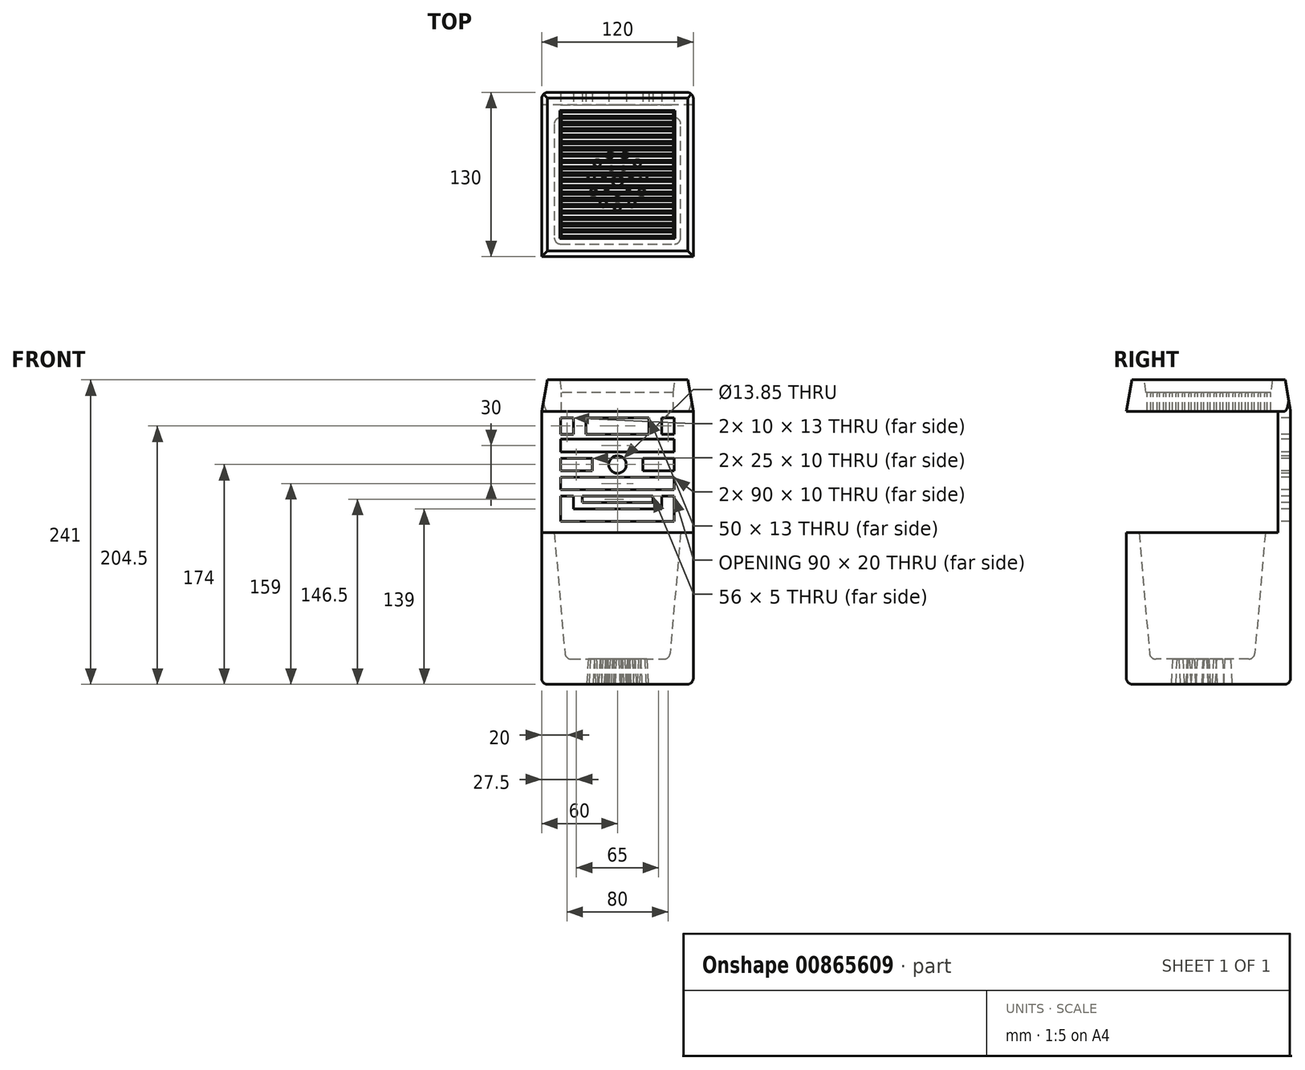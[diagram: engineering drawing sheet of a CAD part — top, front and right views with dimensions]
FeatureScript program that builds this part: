
annotation { "Feature Type Name" : "Feature", "Feature Type Description" : "" }
export const myFeature = defineFeature(function(context is Context, id is Id, definition is map)
    precondition{}
    {
        {
            assignVariable(context, id + "F0", {"name" : "length", "anyValue" : 120});
        }
        {
            var Q0;
            Q0=qCreatedBy(makeId("Top.planeOp"),FACE);
            var sketch = newSketch(context, id + "F1", { "sketchPlane" : qUnion([Q0])});
            skLineSegment(sketch, "E0.bottom", {"start": v(60, 60) * mm, "end": v(-60, 60) * mm});
            skLineSegment(sketch, "E0.top", {"start": v(60, -60) * mm, "end": v(-60, -60) * mm});
            skLineSegment(sketch, "E0.left", {"start": v(60, 60) * mm, "end": v(60, -60) * mm});
            skLineSegment(sketch, "E0.right", {"start": v(-60, 60) * mm, "end": v(-60, -60) * mm});
            skPoint(sketch, "E0.middle", {"position": v(0, 0) * mm});
            skSolve(sketch);
        }
        {
            var Q0;
            Q0=makeQuery(id+"F1.imprint","IMPRINT",FACE,{"disambiguationData":[TD([[makeQuery(id+"F1.imprint","IMPRINT",EDGE,{"derivedFrom":sQuery(id+"F1.wireOp",EDGE,"E0.bottom")}),1.0]])]});
            extrude(context, id + "F2", {"entities" : qUnion([Q0]), "depth" : (getVariable(context, 'length')) * mm, "offsetDistance" : 25 * mm});
        }
        {
            var Q0;
            Q0=makeQuery(id+"F2.opExtrude","SWEPT_FACE",FACE,{"disambiguationData":[OSD([sQuery(id+"F1.wireOp",EDGE,"E0.bottom")])]});
            var sketch = newSketch(context, id + "F3", { "sketchPlane" : qUnion([Q0])});
            skLineSegment(sketch, "E1.bottom", {"start": v(-60, 0) * mm, "end": v(60, 0) * mm});
            skLineSegment(sketch, "E1.top", {"start": v(-60, 216) * mm, "end": v(60, 216) * mm});
            skLineSegment(sketch, "E1.left", {"start": v(-60, 0) * mm, "end": v(-60, 216) * mm});
            skLineSegment(sketch, "E1.right", {"start": v(60, 0) * mm, "end": v(60, 216) * mm});
            skSolve(sketch);
        }
        {
            var Q0;
            Q0=makeQuery(id+"F2.opExtrude","CAP_FACE",FACE,{"disambiguationData":[OSD([sQuery(id+"F1.wireOp",EDGE,"E0.bottom"),sQuery(id+"F1.wireOp",EDGE,"E0.top"),sQuery(id+"F1.wireOp",EDGE,"E0.left"),sQuery(id+"F1.wireOp",EDGE,"E0.right")])],"isStart":false});
            var sketch = newSketch(context, id + "F4", { "sketchPlane" : qUnion([Q0])});
            skLineSegment(sketch, "E2.bottom", {"start": v(50, 50) * mm, "end": v(-50, 50) * mm});
            skLineSegment(sketch, "E2.top", {"start": v(50, -50) * mm, "end": v(-50, -50) * mm});
            skLineSegment(sketch, "E2.left", {"start": v(50, 50) * mm, "end": v(50, -50) * mm});
            skLineSegment(sketch, "E2.right", {"start": v(-50, 50) * mm, "end": v(-50, -50) * mm});
            skPoint(sketch, "E2.middle", {"position": v(0, 0) * mm});
            skSolve(sketch);
        }
        {
            var Q0;
            Q0=makeQuery(id+"F4.imprint","IMPRINT",FACE,{"disambiguationData":[TD([[makeQuery(id+"F4.imprint","IMPRINT",EDGE,{"derivedFrom":sQuery(id+"F4.wireOp",EDGE,"E2.bottom")}),1.0]])]});
            extrude(context, id + "F5", {"entities" : qUnion([Q0]), "operationType" : NewBodyOperationType.REMOVE, "oppositeDirection" : true, "depth" : 100 * mm, "offsetDistance" : 25 * mm, "hasDraft" : true, "draftAngle" : 5 * degree, "draftPullDirection" : true});
        }
        {
            var Q0;
            {var subQ0=sQuery(id+"F3.wireOp",EDGE,"E1.bottom");Q0=makeQuery(id+"F3.imprint","IMPRINT",FACE,{"disambiguationData":[TD([[makeQuery(id+"F3.imprint","IMPRINT",EDGE,{"derivedFrom":subQ0}),1.0]])]});}
            var Q1;
            {var subQ0=sQuery(id+"F3.wireOp",EDGE,"E1.top");Q1=makeQuery(id+"F3.imprint","IMPRINT",FACE,{"disambiguationData":[TD([[makeQuery(id+"F3.imprint","IMPRINT",EDGE,{"derivedFrom":subQ0}),-1.0]])]});}
            extrude(context, id + "F6", {"entities" : qUnion([Q0, Q1]), "operationType" : NewBodyOperationType.ADD, "depth" : 10 * mm, "offsetDistance" : 25 * mm});
        }
        {
            var Q0;
            Q0=makeQuery(id+"F6.opExtrude","CAP_FACE",FACE,{"disambiguationData":[OSD([sQuery(id+"F3.wireOp",EDGE,"E1.bottom"),sQuery(id+"F3.wireOp",EDGE,"E1.top"),sQuery(id+"F3.wireOp",EDGE,"E1.left"),sQuery(id+"F3.wireOp",EDGE,"E1.right")])],"isStart":true});
            var sketch = newSketch(context, id + "F7", { "sketchPlane" : qUnion([Q0])});
            skLineSegment(sketch, "E3", {"start": v(0, 223.83) * mm, "end": v(0, 211) * mm, "construction": true});
            skPoint(sketch, "E3.startSnap0", {"position": v(0, 216) * mm});
            skLineSegment(sketch, "E4.bottom", {"start": v(0, 194) * mm, "end": v(-45, 194) * mm});
            skLineSegment(sketch, "E4.top", {"start": v(0, 184) * mm, "end": v(-45, 184) * mm});
            skLineSegment(sketch, "E4.left", {"start": v(0, 194) * mm, "end": v(0, 184) * mm});
            skLineSegment(sketch, "E4.right", {"start": v(-45, 194) * mm, "end": v(-45, 184) * mm});
            skLineSegment(sketch, "E5.bottom", {"start": v(-45, 179) * mm, "end": v(-20, 179) * mm});
            skLineSegment(sketch, "E5.top", {"start": v(-45, 169) * mm, "end": v(-20, 169) * mm});
            skLineSegment(sketch, "E5.left", {"start": v(-45, 179) * mm, "end": v(-45, 169) * mm});
            skLineSegment(sketch, "E5.right", {"start": v(-20, 179) * mm, "end": v(-20, 169) * mm});
            skLineSegment(sketch, "E6.bottom", {"start": v(-45, 164) * mm, "end": v(0, 164) * mm});
            skLineSegment(sketch, "E6.top", {"start": v(-45, 154) * mm, "end": v(0, 154) * mm});
            skLineSegment(sketch, "E6.left", {"start": v(-45, 164) * mm, "end": v(-45, 154) * mm});
            skLineSegment(sketch, "E6.right", {"start": v(0, 164) * mm, "end": v(0, 154) * mm});
            skLineSegment(sketch, "E7.bottom", {"start": v(-45, 149) * mm, "end": v(-35, 149) * mm});
            skLineSegment(sketch, "E7.top", {"start": v(-45, 129) * mm, "end": v(-35, 129) * mm});
            skLineSegment(sketch, "E7.left", {"start": v(-45, 149) * mm, "end": v(-45, 129) * mm});
            skLineSegment(sketch, "E7.right", {"start": v(-35, 149) * mm, "end": v(-35, 139) * mm});
            skLineSegment(sketch, "E8.bottom", {"start": v(-35, 139) * mm, "end": v(0, 139) * mm});
            skLineSegment(sketch, "E8.top", {"start": v(-35, 129) * mm, "end": v(0, 129) * mm});
            skLineSegment(sketch, "E8.right", {"start": v(0, 139) * mm, "end": v(0, 129) * mm});
            skLineSegment(sketch, "E9.bottom", {"start": v(-28, 149) * mm, "end": v(0, 149) * mm});
            skLineSegment(sketch, "E9.top", {"start": v(-28, 144) * mm, "end": v(0, 144) * mm});
            skLineSegment(sketch, "E9.left", {"start": v(-28, 149) * mm, "end": v(-28, 144) * mm});
            skLineSegment(sketch, "E9.right", {"start": v(0, 149) * mm, "end": v(0, 144) * mm});
            skLineSegment(sketch, "E10.bottom", {"start": v(-45, 211) * mm, "end": v(-35, 211) * mm});
            skLineSegment(sketch, "E10.top", {"start": v(-45, 198) * mm, "end": v(-35, 198) * mm});
            skLineSegment(sketch, "E10.left", {"start": v(-45, 211) * mm, "end": v(-45, 198) * mm});
            skLineSegment(sketch, "E10.right", {"start": v(-35, 211) * mm, "end": v(-35, 198) * mm});
            skLineSegment(sketch, "E11.bottom", {"start": v(0, 211) * mm, "end": v(-25, 211) * mm});
            skLineSegment(sketch, "E11.top", {"start": v(0, 198) * mm, "end": v(-25, 198) * mm});
            skLineSegment(sketch, "E11.left", {"start": v(0, 211) * mm, "end": v(0, 198) * mm});
            skLineSegment(sketch, "E11.right", {"start": v(-25, 211) * mm, "end": v(-25, 198) * mm});
            skArc(sketch, "E12", {"start": v(0, 180.92) * mm, "mid": v(-6.92, 174) * mm, "end": v(0, 167.08) * mm});
            skPoint(sketch, "E12.centerSnap0", {"position": v(-20, 174) * mm});
            skLineSegment(sketch, "E13.trimOffspring", {"start": v(0, 154) * mm, "end": v(0, 149) * mm, "construction": true});
            skLineSegment(sketch, "E14.trimOffspring", {"start": v(0, 144) * mm, "end": v(0, 139) * mm, "construction": true});
            skLineSegment(sketch, "E15.trimOffspring", {"start": v(0, 129) * mm, "end": v(0, 105.75) * mm, "construction": true});
            skLineSegment(sketch, "E16.trimOffspring", {"start": v(0, 184) * mm, "end": v(0, 164) * mm, "construction": true});
            skLineSegment(sketch, "E17.trimOffspring", {"start": v(0, 198) * mm, "end": v(0, 194) * mm, "construction": true});
            skArc(sketch, "E18.MirrorCS", {"start": v(0, 180.92) * mm, "mid": v(6.92, 174) * mm, "end": v(0, 167.08) * mm});
            skLineSegment(sketch, "E19.MirrorCS", {"start": v(28, 149) * mm, "end": v(28, 144) * mm});
            skLineSegment(sketch, "E20.MirrorCS", {"start": v(20, 179) * mm, "end": v(20, 169) * mm});
            skLineSegment(sketch, "E21.MirrorCS", {"start": v(35, 211) * mm, "end": v(35, 198) * mm});
            skLineSegment(sketch, "E22.MirrorCS", {"start": v(45, 169) * mm, "end": v(20, 169) * mm});
            skPoint(sketch, "E23.MirrorP", {"position": v(20, 174) * mm});
            skLineSegment(sketch, "E24.MirrorCS", {"start": v(45, 179) * mm, "end": v(20, 179) * mm});
            skLineSegment(sketch, "E25.MirrorCS", {"start": v(0, 211) * mm, "end": v(25, 211) * mm});
            skLineSegment(sketch, "E26.MirrorCS", {"start": v(28, 144) * mm, "end": v(0, 144) * mm});
            skLineSegment(sketch, "E27.MirrorCS", {"start": v(45, 154) * mm, "end": v(0, 154) * mm});
            skLineSegment(sketch, "E28.MirrorCS", {"start": v(45, 129) * mm, "end": v(35, 129) * mm});
            skLineSegment(sketch, "E29.MirrorCS", {"start": v(45, 179) * mm, "end": v(45, 169) * mm});
            skLineSegment(sketch, "E30.MirrorCS", {"start": v(0, 194) * mm, "end": v(45, 194) * mm});
            skLineSegment(sketch, "E31.MirrorCS", {"start": v(45, 149) * mm, "end": v(35, 149) * mm});
            skLineSegment(sketch, "E32.MirrorCS", {"start": v(35, 149) * mm, "end": v(35, 139) * mm});
            skLineSegment(sketch, "E33.MirrorCS", {"start": v(45, 211) * mm, "end": v(35, 211) * mm});
            skLineSegment(sketch, "E34.MirrorCS", {"start": v(25, 211) * mm, "end": v(25, 198) * mm});
            skLineSegment(sketch, "E35.MirrorCS", {"start": v(45, 198) * mm, "end": v(35, 198) * mm});
            skLineSegment(sketch, "E36.MirrorCS", {"start": v(35, 129) * mm, "end": v(0, 129) * mm});
            skLineSegment(sketch, "E37.MirrorCS", {"start": v(45, 164) * mm, "end": v(0, 164) * mm});
            skLineSegment(sketch, "E38.MirrorCS", {"start": v(35, 139) * mm, "end": v(0, 139) * mm});
            skLineSegment(sketch, "E39.MirrorCS", {"start": v(28, 149) * mm, "end": v(0, 149) * mm});
            skLineSegment(sketch, "E40.MirrorCS", {"start": v(0, 184) * mm, "end": v(45, 184) * mm});
            skLineSegment(sketch, "E41.MirrorCS", {"start": v(45, 164) * mm, "end": v(45, 154) * mm});
            skLineSegment(sketch, "E42.MirrorCS", {"start": v(45, 211) * mm, "end": v(45, 198) * mm});
            skLineSegment(sketch, "E43.MirrorCS", {"start": v(0, 198) * mm, "end": v(25, 198) * mm});
            skLineSegment(sketch, "E44.MirrorCS", {"start": v(45, 149) * mm, "end": v(45, 129) * mm});
            skLineSegment(sketch, "E45.MirrorCS", {"start": v(45, 194) * mm, "end": v(45, 184) * mm});
            skSolve(sketch);
        }
        {
            var Q0;
            Q0=makeQuery(id+"F7.imprint","IMPRINT",FACE,{"disambiguationData":[TD([[makeQuery(id+"F7.imprint","IMPRINT",EDGE,{"derivedFrom":sQuery(id+"F7.wireOp",EDGE,"E7.bottom")}),-1.0]])]});
            var Q1;
            Q1=makeQuery(id+"F7.imprint","IMPRINT",FACE,{"disambiguationData":[TD([[makeQuery(id+"F7.imprint","IMPRINT",EDGE,{"derivedFrom":sQuery(id+"F7.wireOp",EDGE,"E9.bottom")}),-1.0]])]});
            var Q2;
            Q2=makeQuery(id+"F7.imprint","IMPRINT",FACE,{"disambiguationData":[TD([[makeQuery(id+"F7.imprint","IMPRINT",EDGE,{"derivedFrom":sQuery(id+"F7.wireOp",EDGE,"E8.right")}),1.0]])]});
            var Q3;
            Q3=makeQuery(id+"F7.imprint","IMPRINT",FACE,{"disambiguationData":[TD([[makeQuery(id+"F7.imprint","IMPRINT",EDGE,{"derivedFrom":sQuery(id+"F7.wireOp",EDGE,"E9.right")}),1.0]])]});
            var Q4;
            Q4=makeQuery(id+"F7.imprint","IMPRINT",FACE,{"disambiguationData":[TD([[makeQuery(id+"F7.imprint","IMPRINT",EDGE,{"derivedFrom":sQuery(id+"F7.wireOp",EDGE,"E6.bottom")}),-1.0]])]});
            var Q5;
            Q5=makeQuery(id+"F7.imprint","IMPRINT",FACE,{"disambiguationData":[TD([[makeQuery(id+"F7.imprint","IMPRINT",EDGE,{"derivedFrom":sQuery(id+"F7.wireOp",EDGE,"E5.bottom")}),-1.0]])]});
            var Q6;
            Q6=makeQuery(id+"F7.imprint","IMPRINT",FACE,{"disambiguationData":[TD([[makeQuery(id+"F7.imprint","IMPRINT",EDGE,{"derivedFrom":sQuery(id+"F7.wireOp",EDGE,"E4.bottom")}),1.0]])]});
            var Q7;
            Q7=makeQuery(id+"F7.imprint","IMPRINT",FACE,{"disambiguationData":[TD([[makeQuery(id+"F7.imprint","IMPRINT",EDGE,{"derivedFrom":sQuery(id+"F7.wireOp",EDGE,"E10.bottom")}),-1.0]])]});
            var Q8;
            Q8=makeQuery(id+"F7.imprint","IMPRINT",FACE,{"disambiguationData":[TD([[makeQuery(id+"F7.imprint","IMPRINT",EDGE,{"derivedFrom":sQuery(id+"F7.wireOp",EDGE,"E11.bottom")}),1.0]])]});
            var Q9;
            Q9=makeQuery(id+"F7.imprint","IMPRINT",FACE,{"disambiguationData":[TD([[makeQuery(id+"F7.imprint","IMPRINT",EDGE,{"derivedFrom":sQuery(id+"F7.wireOp",EDGE,"E11.left")}),1.0]])]});
            var Q10;
            Q10=makeQuery(id+"F7.imprint","IMPRINT",FACE,{"disambiguationData":[TD([[makeQuery(id+"F7.imprint","IMPRINT",EDGE,{"derivedFrom":sQuery(id+"F7.wireOp",EDGE,"E21.MirrorCS")}),1.0]])]});
            var Q11;
            Q11=makeQuery(id+"F7.imprint","IMPRINT",FACE,{"disambiguationData":[TD([[makeQuery(id+"F7.imprint","IMPRINT",EDGE,{"derivedFrom":sQuery(id+"F7.wireOp",EDGE,"E4.left")}),1.0]])]});
            var Q12;
            Q12=makeQuery(id+"F7.imprint","IMPRINT",FACE,{"disambiguationData":[TD([[makeQuery(id+"F7.imprint","IMPRINT",EDGE,{"derivedFrom":sQuery(id+"F7.wireOp",EDGE,"E20.MirrorCS")}),1.0]])]});
            var Q13;
            Q13=makeQuery(id+"F7.imprint","IMPRINT",FACE,{"disambiguationData":[TD([[makeQuery(id+"F7.imprint","IMPRINT",EDGE,{"derivedFrom":sQuery(id+"F7.wireOp",EDGE,"E12")}),1.0]])]});
            var Q14;
            Q14=makeQuery(id+"F7.imprint","IMPRINT",FACE,{"disambiguationData":[TD([[makeQuery(id+"F7.imprint","IMPRINT",EDGE,{"derivedFrom":sQuery(id+"F7.wireOp",EDGE,"E6.right")}),1.0]])]});
            var Q15;
            Q15=makeQuery(id+"F6.opExtrude","CAP_FACE",FACE,{"disambiguationData":[OSD([sQuery(id+"F3.wireOp",EDGE,"E1.bottom"),sQuery(id+"F3.wireOp",EDGE,"E1.top"),sQuery(id+"F3.wireOp",EDGE,"E1.left"),sQuery(id+"F3.wireOp",EDGE,"E1.right")])],"isStart":false});
            extrude(context, id + "F8", {"entities" : qUnion([Q0, Q1, Q2, Q3, Q4, Q5, Q6, Q7, Q8, Q9, Q10, Q11, Q12, Q13, Q14]), "operationType" : NewBodyOperationType.REMOVE, "endBound" : BoundingType.UP_TO_SURFACE, "oppositeDirection" : true, "depth" : 25 * mm, "endBoundEntityFace" : qUnion([Q15]), "offsetDistance" : 25 * mm});
        }
        {
            var Q0;
            Q0=makeQuery(id+"F6.opExtrude","SWEPT_FACE",FACE,{"disambiguationData":[OSD([sQuery(id+"F3.wireOp",EDGE,"E1.top")])]});
            var sketch = newSketch(context, id + "F9", { "sketchPlane" : qUnion([Q0])});
            skLineSegment(sketch, "E46.bottom", {"start": v(-60, 70) * mm, "end": v(60, 70) * mm});
            skLineSegment(sketch, "E46.top", {"start": v(-60, -60) * mm, "end": v(60, -60) * mm});
            skLineSegment(sketch, "E46.left", {"start": v(-60, 70) * mm, "end": v(-60, -60) * mm});
            skLineSegment(sketch, "E46.right", {"start": v(60, 70) * mm, "end": v(60, -60) * mm});
            skSolve(sketch);
        }
        {
            var Q0;
            Q0 = qSketchRegion(id + "F9", true);
            extrude(context, id + "F10", {"entities" : qUnion([Q0]), "operationType" : NewBodyOperationType.ADD, "depth" : 25 * mm, "offsetDistance" : 25 * mm, "hasDraft" : true, "draftAngle" : 10 * degree, "draftPullDirection" : true});
        }
        {
            var Q0;
            Q0=makeQuery(id+"F10.opExtrude","CAP_FACE",FACE,{"disambiguationData":[OSD([sQuery(id+"F9.wireOp",EDGE,"E46.bottom"),sQuery(id+"F9.wireOp",EDGE,"E46.top"),sQuery(id+"F9.wireOp",EDGE,"E46.left"),sQuery(id+"F9.wireOp",EDGE,"E46.right")])],"isStart":false});
            var sketch = newSketch(context, id + "F11", { "sketchPlane" : qUnion([Q0])});
            skLineSegment(sketch, "E47.bottom", {"start": v(-45.6, 55.6) * mm, "end": v(45.6, 55.6) * mm});
            skLineSegment(sketch, "E47.top", {"start": v(-45.6, -45.6) * mm, "end": v(45.6, -45.6) * mm});
            skLineSegment(sketch, "E47.left", {"start": v(-45.6, 55.6) * mm, "end": v(-45.6, -45.6) * mm});
            skLineSegment(sketch, "E47.right", {"start": v(45.6, 55.6) * mm, "end": v(45.6, -45.6) * mm});
            skSolve(sketch);
        }
        {
            var Q0;
            Q0=makeQuery(id+"F11.imprint","IMPRINT",FACE,{"disambiguationData":[TD([[makeQuery(id+"F11.imprint","IMPRINT",EDGE,{"derivedFrom":sQuery(id+"F11.wireOp",EDGE,"E47.bottom")}),-1.0]])]});
            extrude(context, id + "F12", {"entities" : qUnion([Q0]), "operationType" : NewBodyOperationType.REMOVE, "oppositeDirection" : true, "depth" : 10 * mm, "offsetDistance" : 25 * mm, "hasDraft" : true, "draftAngle" : 7 * degree, "draftPullDirection" : true});
        }
        {
            var Q0;
            Q0=makeQuery(id+"F12.boolean.opBoolean","COPY",FACE,{"derivedFrom":makeQuery(id+"F12.opExtrude","CAP_FACE",FACE,{"disambiguationData":[OSD([sQuery(id+"F11.wireOp",EDGE,"E47.bottom"),sQuery(id+"F11.wireOp",EDGE,"E47.top"),sQuery(id+"F11.wireOp",EDGE,"E47.left"),sQuery(id+"F11.wireOp",EDGE,"E47.right")])],"isStart":false})});
            var sketch = newSketch(context, id + "F13", { "sketchPlane" : qUnion([Q0])});
            skLineSegment(sketch, "E48.bottom", {"start": v(-44.36, 54.36) * mm, "end": v(44.36, 54.36) * mm});
            skLineSegment(sketch, "E48.top", {"start": v(-44.36, 51.36) * mm, "end": v(44.36, 51.36) * mm});
            skLineSegment(sketch, "E48.left", {"start": v(-44.36, 54.36) * mm, "end": v(-44.36, 51.36) * mm});
            skLineSegment(sketch, "E48.right", {"start": v(44.36, 54.36) * mm, "end": v(44.36, 51.36) * mm});
            skLineSegment(sketch, "E49.0.1.0", {"start": v(-44.36, 46.36) * mm, "end": v(44.36, 46.36) * mm});
            skLineSegment(sketch, "E49.0.1.1", {"start": v(44.36, 49.36) * mm, "end": v(44.36, 46.36) * mm});
            skLineSegment(sketch, "E49.0.1.2", {"start": v(-44.36, 49.36) * mm, "end": v(44.36, 49.36) * mm});
            skLineSegment(sketch, "E49.0.1.3", {"start": v(-44.36, 49.36) * mm, "end": v(-44.36, 46.36) * mm});
            skLineSegment(sketch, "E49.0.2.0", {"start": v(-44.36, 41.36) * mm, "end": v(44.36, 41.36) * mm});
            skLineSegment(sketch, "E49.0.2.1", {"start": v(44.36, 44.36) * mm, "end": v(44.36, 41.36) * mm});
            skLineSegment(sketch, "E49.0.2.2", {"start": v(-44.36, 44.36) * mm, "end": v(44.36, 44.36) * mm});
            skLineSegment(sketch, "E49.0.2.3", {"start": v(-44.36, 44.36) * mm, "end": v(-44.36, 41.36) * mm});
            skLineSegment(sketch, "E49.0.3.0", {"start": v(-44.36, 36.36) * mm, "end": v(44.36, 36.36) * mm});
            skLineSegment(sketch, "E49.0.3.1", {"start": v(44.36, 39.36) * mm, "end": v(44.36, 36.36) * mm});
            skLineSegment(sketch, "E49.0.3.2", {"start": v(-44.36, 39.36) * mm, "end": v(44.36, 39.36) * mm});
            skLineSegment(sketch, "E49.0.3.3", {"start": v(-44.36, 39.36) * mm, "end": v(-44.36, 36.36) * mm});
            skLineSegment(sketch, "E49.0.4.0", {"start": v(-44.36, 31.36) * mm, "end": v(44.36, 31.36) * mm});
            skLineSegment(sketch, "E49.0.4.1", {"start": v(44.36, 34.36) * mm, "end": v(44.36, 31.36) * mm});
            skLineSegment(sketch, "E49.0.4.2", {"start": v(-44.36, 34.36) * mm, "end": v(44.36, 34.36) * mm});
            skLineSegment(sketch, "E49.0.4.3", {"start": v(-44.36, 34.36) * mm, "end": v(-44.36, 31.36) * mm});
            skLineSegment(sketch, "E49.0.5.0", {"start": v(-44.36, 26.36) * mm, "end": v(44.36, 26.36) * mm});
            skLineSegment(sketch, "E49.0.5.1", {"start": v(44.36, 29.36) * mm, "end": v(44.36, 26.36) * mm});
            skLineSegment(sketch, "E49.0.5.2", {"start": v(-44.36, 29.36) * mm, "end": v(44.36, 29.36) * mm});
            skLineSegment(sketch, "E49.0.5.3", {"start": v(-44.36, 29.36) * mm, "end": v(-44.36, 26.36) * mm});
            skLineSegment(sketch, "E49.0.6.0", {"start": v(-44.36, 21.36) * mm, "end": v(44.36, 21.36) * mm});
            skLineSegment(sketch, "E49.0.6.1", {"start": v(44.36, 24.36) * mm, "end": v(44.36, 21.36) * mm});
            skLineSegment(sketch, "E49.0.6.2", {"start": v(-44.36, 24.36) * mm, "end": v(44.36, 24.36) * mm});
            skLineSegment(sketch, "E49.0.6.3", {"start": v(-44.36, 24.36) * mm, "end": v(-44.36, 21.36) * mm});
            skLineSegment(sketch, "E49.0.7.0", {"start": v(-44.36, 16.36) * mm, "end": v(44.36, 16.36) * mm});
            skLineSegment(sketch, "E49.0.7.1", {"start": v(44.36, 19.36) * mm, "end": v(44.36, 16.36) * mm});
            skLineSegment(sketch, "E49.0.7.2", {"start": v(-44.36, 19.36) * mm, "end": v(44.36, 19.36) * mm});
            skLineSegment(sketch, "E49.0.7.3", {"start": v(-44.36, 19.36) * mm, "end": v(-44.36, 16.36) * mm});
            skLineSegment(sketch, "E49.0.8.0", {"start": v(-44.36, 11.36) * mm, "end": v(44.36, 11.36) * mm});
            skLineSegment(sketch, "E49.0.8.1", {"start": v(44.36, 14.36) * mm, "end": v(44.36, 11.36) * mm});
            skLineSegment(sketch, "E49.0.8.2", {"start": v(-44.36, 14.36) * mm, "end": v(44.36, 14.36) * mm});
            skLineSegment(sketch, "E49.0.8.3", {"start": v(-44.36, 14.36) * mm, "end": v(-44.36, 11.36) * mm});
            skLineSegment(sketch, "E49.0.9.0", {"start": v(-44.36, 6.36) * mm, "end": v(44.36, 6.36) * mm});
            skLineSegment(sketch, "E49.0.9.1", {"start": v(44.36, 9.36) * mm, "end": v(44.36, 6.36) * mm});
            skLineSegment(sketch, "E49.0.9.2", {"start": v(-44.36, 9.36) * mm, "end": v(44.36, 9.36) * mm});
            skLineSegment(sketch, "E49.0.9.3", {"start": v(-44.36, 9.36) * mm, "end": v(-44.36, 6.36) * mm});
            skLineSegment(sketch, "E49.0.10.0", {"start": v(-44.36, 1.36) * mm, "end": v(44.36, 1.36) * mm});
            skLineSegment(sketch, "E49.0.10.1", {"start": v(44.36, 4.36) * mm, "end": v(44.36, 1.36) * mm});
            skLineSegment(sketch, "E49.0.10.2", {"start": v(-44.36, 4.36) * mm, "end": v(44.36, 4.36) * mm});
            skLineSegment(sketch, "E49.0.10.3", {"start": v(-44.36, 4.36) * mm, "end": v(-44.36, 1.36) * mm});
            skLineSegment(sketch, "E49.0.11.0", {"start": v(-44.36, -3.64) * mm, "end": v(44.36, -3.64) * mm});
            skLineSegment(sketch, "E49.0.11.1", {"start": v(44.36, -0.64) * mm, "end": v(44.36, -3.64) * mm});
            skLineSegment(sketch, "E49.0.11.2", {"start": v(-44.36, -0.64) * mm, "end": v(44.36, -0.64) * mm});
            skLineSegment(sketch, "E49.0.11.3", {"start": v(-44.36, -0.64) * mm, "end": v(-44.36, -3.64) * mm});
            skLineSegment(sketch, "E49.0.12.0", {"start": v(-44.36, -8.64) * mm, "end": v(44.36, -8.64) * mm});
            skLineSegment(sketch, "E49.0.12.1", {"start": v(44.36, -5.64) * mm, "end": v(44.36, -8.64) * mm});
            skLineSegment(sketch, "E49.0.12.2", {"start": v(-44.36, -5.64) * mm, "end": v(44.36, -5.64) * mm});
            skLineSegment(sketch, "E49.0.12.3", {"start": v(-44.36, -5.64) * mm, "end": v(-44.36, -8.64) * mm});
            skLineSegment(sketch, "E49.0.13.0", {"start": v(-44.36, -13.64) * mm, "end": v(44.36, -13.64) * mm});
            skLineSegment(sketch, "E49.0.13.1", {"start": v(44.36, -10.64) * mm, "end": v(44.36, -13.64) * mm});
            skLineSegment(sketch, "E49.0.13.2", {"start": v(-44.36, -10.64) * mm, "end": v(44.36, -10.64) * mm});
            skLineSegment(sketch, "E49.0.13.3", {"start": v(-44.36, -10.64) * mm, "end": v(-44.36, -13.64) * mm});
            skLineSegment(sketch, "E49.0.14.0", {"start": v(-44.36, -18.64) * mm, "end": v(44.36, -18.64) * mm});
            skLineSegment(sketch, "E49.0.14.1", {"start": v(44.36, -15.64) * mm, "end": v(44.36, -18.64) * mm});
            skLineSegment(sketch, "E49.0.14.2", {"start": v(-44.36, -15.64) * mm, "end": v(44.36, -15.64) * mm});
            skLineSegment(sketch, "E49.0.14.3", {"start": v(-44.36, -15.64) * mm, "end": v(-44.36, -18.64) * mm});
            skLineSegment(sketch, "E49.0.15.0", {"start": v(-44.36, -23.64) * mm, "end": v(44.36, -23.64) * mm});
            skLineSegment(sketch, "E49.0.15.1", {"start": v(44.36, -20.64) * mm, "end": v(44.36, -23.64) * mm});
            skLineSegment(sketch, "E49.0.15.2", {"start": v(-44.36, -20.64) * mm, "end": v(44.36, -20.64) * mm});
            skLineSegment(sketch, "E49.0.15.3", {"start": v(-44.36, -20.64) * mm, "end": v(-44.36, -23.64) * mm});
            skLineSegment(sketch, "E49.0.16.0", {"start": v(-44.36, -28.64) * mm, "end": v(44.36, -28.64) * mm});
            skLineSegment(sketch, "E49.0.16.1", {"start": v(44.36, -25.64) * mm, "end": v(44.36, -28.64) * mm});
            skLineSegment(sketch, "E49.0.16.2", {"start": v(-44.36, -25.64) * mm, "end": v(44.36, -25.64) * mm});
            skLineSegment(sketch, "E49.0.16.3", {"start": v(-44.36, -25.64) * mm, "end": v(-44.36, -28.64) * mm});
            skLineSegment(sketch, "E49.0.17.0", {"start": v(-44.36, -33.64) * mm, "end": v(44.36, -33.64) * mm});
            skLineSegment(sketch, "E49.0.17.1", {"start": v(44.36, -30.64) * mm, "end": v(44.36, -33.64) * mm});
            skLineSegment(sketch, "E49.0.17.2", {"start": v(-44.36, -30.64) * mm, "end": v(44.36, -30.64) * mm});
            skLineSegment(sketch, "E49.0.17.3", {"start": v(-44.36, -30.64) * mm, "end": v(-44.36, -33.64) * mm});
            skLineSegment(sketch, "E49.0.18.0", {"start": v(-44.36, -38.64) * mm, "end": v(44.36, -38.64) * mm});
            skLineSegment(sketch, "E49.0.18.1", {"start": v(44.36, -35.64) * mm, "end": v(44.36, -38.64) * mm});
            skLineSegment(sketch, "E49.0.18.2", {"start": v(-44.36, -35.64) * mm, "end": v(44.36, -35.64) * mm});
            skLineSegment(sketch, "E49.0.18.3", {"start": v(-44.36, -35.64) * mm, "end": v(-44.36, -38.64) * mm});
            skLineSegment(sketch, "E49.direction1", {"start": v(-44.36, 51.36) * mm, "end": v(-19.36, 51.36) * mm, "construction": true});
            skLineSegment(sketch, "E49.direction2", {"start": v(-44.36, 51.36) * mm, "end": v(-44.36, 46.36) * mm, "construction": true});
            skLineSegment(sketch, "E50.0.0.19", {"start": v(-44.36, -43.64) * mm, "end": v(44.36, -43.64) * mm});
            skLineSegment(sketch, "E50.3.0.19", {"start": v(44.36, -40.64) * mm, "end": v(44.36, -43.64) * mm});
            skLineSegment(sketch, "E50.6.0.19", {"start": v(-44.36, -40.64) * mm, "end": v(44.36, -40.64) * mm});
            skLineSegment(sketch, "E50.9.0.19", {"start": v(-44.36, -40.64) * mm, "end": v(-44.36, -43.64) * mm});
            skSolve(sketch);
        }
        {
            var Q0;
            Q0 = qSketchRegion(id + "F13", true);
            var Q1;
            Q1=makeQuery(id+"F10.opExtrude","CAP_FACE",FACE,{"disambiguationData":[OSD([sQuery(id+"F9.wireOp",EDGE,"E46.bottom"),sQuery(id+"F9.wireOp",EDGE,"E46.top"),sQuery(id+"F9.wireOp",EDGE,"E46.left"),sQuery(id+"F9.wireOp",EDGE,"E46.right")])],"isStart":true});
            extrude(context, id + "F14", {"entities" : qUnion([Q0]), "operationType" : NewBodyOperationType.REMOVE, "endBound" : BoundingType.UP_TO_SURFACE, "oppositeDirection" : true, "depth" : 25 * mm, "endBoundEntityFace" : qUnion([Q1]), "offsetDistance" : 25 * mm});
        }
        {
            var Q0;
            Q0=makeQuery(id+"F14.boolean.opBoolean","COPY",EDGE,{"derivedFrom":makeQuery(id+"F14.opExtrude","CAP_EDGE",EDGE,{"disambiguationData":[OSD([sQuery(id+"F13.wireOp",EDGE,"E48.top")])],"isStart":true})});
            var Q1;
            Q1=makeQuery(id+"F14.boolean.opBoolean","COPY",EDGE,{"derivedFrom":makeQuery(id+"F14.opExtrude","CAP_EDGE",EDGE,{"disambiguationData":[OSD([sQuery(id+"F13.wireOp",EDGE,"E49.0.1.2")])],"isStart":true})});
            var Q2;
            Q2=makeQuery(id+"F14.boolean.opBoolean","COPY",EDGE,{"derivedFrom":makeQuery(id+"F14.opExtrude","CAP_EDGE",EDGE,{"disambiguationData":[OSD([sQuery(id+"F13.wireOp",EDGE,"E49.0.1.0")])],"isStart":true})});
            var Q3;
            Q3=makeQuery(id+"F14.boolean.opBoolean","COPY",EDGE,{"derivedFrom":makeQuery(id+"F14.opExtrude","CAP_EDGE",EDGE,{"disambiguationData":[OSD([sQuery(id+"F13.wireOp",EDGE,"E49.0.2.2")])],"isStart":true})});
            var Q4;
            Q4=makeQuery(id+"F14.boolean.opBoolean","COPY",EDGE,{"derivedFrom":makeQuery(id+"F14.opExtrude","CAP_EDGE",EDGE,{"disambiguationData":[OSD([sQuery(id+"F13.wireOp",EDGE,"E49.0.2.0")])],"isStart":true})});
            var Q5;
            Q5=makeQuery(id+"F14.boolean.opBoolean","COPY",EDGE,{"derivedFrom":makeQuery(id+"F14.opExtrude","CAP_EDGE",EDGE,{"disambiguationData":[OSD([sQuery(id+"F13.wireOp",EDGE,"E49.0.3.2")])],"isStart":true})});
            var Q6;
            Q6=makeQuery(id+"F14.boolean.opBoolean","COPY",EDGE,{"derivedFrom":makeQuery(id+"F14.opExtrude","CAP_EDGE",EDGE,{"disambiguationData":[OSD([sQuery(id+"F13.wireOp",EDGE,"E49.0.3.0")])],"isStart":true})});
            var Q7;
            Q7=makeQuery(id+"F14.boolean.opBoolean","COPY",EDGE,{"derivedFrom":makeQuery(id+"F14.opExtrude","CAP_EDGE",EDGE,{"disambiguationData":[OSD([sQuery(id+"F13.wireOp",EDGE,"E49.0.4.2")])],"isStart":true})});
            var Q8;
            Q8=makeQuery(id+"F14.boolean.opBoolean","COPY",EDGE,{"derivedFrom":makeQuery(id+"F14.opExtrude","CAP_EDGE",EDGE,{"disambiguationData":[OSD([sQuery(id+"F13.wireOp",EDGE,"E49.0.4.0")])],"isStart":true})});
            var Q9;
            Q9=makeQuery(id+"F14.boolean.opBoolean","COPY",EDGE,{"derivedFrom":makeQuery(id+"F14.opExtrude","CAP_EDGE",EDGE,{"disambiguationData":[OSD([sQuery(id+"F13.wireOp",EDGE,"E49.0.5.2")])],"isStart":true})});
            var Q10;
            Q10=makeQuery(id+"F14.boolean.opBoolean","COPY",EDGE,{"derivedFrom":makeQuery(id+"F14.opExtrude","CAP_EDGE",EDGE,{"disambiguationData":[OSD([sQuery(id+"F13.wireOp",EDGE,"E49.0.5.0")])],"isStart":true})});
            var Q11;
            Q11=makeQuery(id+"F14.boolean.opBoolean","COPY",EDGE,{"derivedFrom":makeQuery(id+"F14.opExtrude","CAP_EDGE",EDGE,{"disambiguationData":[OSD([sQuery(id+"F13.wireOp",EDGE,"E49.0.6.2")])],"isStart":true})});
            var Q12;
            Q12=makeQuery(id+"F14.boolean.opBoolean","COPY",EDGE,{"derivedFrom":makeQuery(id+"F14.opExtrude","CAP_EDGE",EDGE,{"disambiguationData":[OSD([sQuery(id+"F13.wireOp",EDGE,"E49.0.6.0")])],"isStart":true})});
            var Q13;
            Q13=makeQuery(id+"F14.boolean.opBoolean","COPY",EDGE,{"derivedFrom":makeQuery(id+"F14.opExtrude","CAP_EDGE",EDGE,{"disambiguationData":[OSD([sQuery(id+"F13.wireOp",EDGE,"E49.0.7.2")])],"isStart":true})});
            var Q14;
            Q14=makeQuery(id+"F14.boolean.opBoolean","COPY",EDGE,{"derivedFrom":makeQuery(id+"F14.opExtrude","CAP_EDGE",EDGE,{"disambiguationData":[OSD([sQuery(id+"F13.wireOp",EDGE,"E49.0.7.0")])],"isStart":true})});
            var Q15;
            Q15=makeQuery(id+"F14.boolean.opBoolean","COPY",EDGE,{"derivedFrom":makeQuery(id+"F14.opExtrude","CAP_EDGE",EDGE,{"disambiguationData":[OSD([sQuery(id+"F13.wireOp",EDGE,"E49.0.8.2")])],"isStart":true})});
            var Q16;
            Q16=makeQuery(id+"F14.boolean.opBoolean","COPY",EDGE,{"derivedFrom":makeQuery(id+"F14.opExtrude","CAP_EDGE",EDGE,{"disambiguationData":[OSD([sQuery(id+"F13.wireOp",EDGE,"E49.0.8.0")])],"isStart":true})});
            var Q17;
            Q17=makeQuery(id+"F14.boolean.opBoolean","COPY",EDGE,{"derivedFrom":makeQuery(id+"F14.opExtrude","CAP_EDGE",EDGE,{"disambiguationData":[OSD([sQuery(id+"F13.wireOp",EDGE,"E49.0.9.2")])],"isStart":true})});
            var Q18;
            Q18=makeQuery(id+"F14.boolean.opBoolean","COPY",EDGE,{"derivedFrom":makeQuery(id+"F14.opExtrude","CAP_EDGE",EDGE,{"disambiguationData":[OSD([sQuery(id+"F13.wireOp",EDGE,"E49.0.12.2")])],"isStart":true})});
            var Q19;
            Q19=makeQuery(id+"F14.boolean.opBoolean","COPY",EDGE,{"derivedFrom":makeQuery(id+"F14.opExtrude","CAP_EDGE",EDGE,{"disambiguationData":[OSD([sQuery(id+"F13.wireOp",EDGE,"E49.0.12.0")])],"isStart":true})});
            var Q20;
            Q20=makeQuery(id+"F14.boolean.opBoolean","COPY",EDGE,{"derivedFrom":makeQuery(id+"F14.opExtrude","CAP_EDGE",EDGE,{"disambiguationData":[OSD([sQuery(id+"F13.wireOp",EDGE,"E49.0.13.2")])],"isStart":true})});
            var Q21;
            Q21=makeQuery(id+"F14.boolean.opBoolean","COPY",EDGE,{"derivedFrom":makeQuery(id+"F14.opExtrude","CAP_EDGE",EDGE,{"disambiguationData":[OSD([sQuery(id+"F13.wireOp",EDGE,"E49.0.13.0")])],"isStart":true})});
            var Q22;
            Q22=makeQuery(id+"F14.boolean.opBoolean","COPY",EDGE,{"derivedFrom":makeQuery(id+"F14.opExtrude","CAP_EDGE",EDGE,{"disambiguationData":[OSD([sQuery(id+"F13.wireOp",EDGE,"E49.0.14.2")])],"isStart":true})});
            var Q23;
            Q23=makeQuery(id+"F14.boolean.opBoolean","COPY",EDGE,{"derivedFrom":makeQuery(id+"F14.opExtrude","CAP_EDGE",EDGE,{"disambiguationData":[OSD([sQuery(id+"F13.wireOp",EDGE,"E49.0.14.0")])],"isStart":true})});
            var Q24;
            Q24=makeQuery(id+"F14.boolean.opBoolean","COPY",EDGE,{"derivedFrom":makeQuery(id+"F14.opExtrude","CAP_EDGE",EDGE,{"disambiguationData":[OSD([sQuery(id+"F13.wireOp",EDGE,"E49.0.15.2")])],"isStart":true})});
            var Q25;
            Q25=makeQuery(id+"F14.boolean.opBoolean","COPY",EDGE,{"derivedFrom":makeQuery(id+"F14.opExtrude","CAP_EDGE",EDGE,{"disambiguationData":[OSD([sQuery(id+"F13.wireOp",EDGE,"E49.0.15.0")])],"isStart":true})});
            var Q26;
            Q26=makeQuery(id+"F14.boolean.opBoolean","COPY",EDGE,{"derivedFrom":makeQuery(id+"F14.opExtrude","CAP_EDGE",EDGE,{"disambiguationData":[OSD([sQuery(id+"F13.wireOp",EDGE,"E49.0.16.2")])],"isStart":true})});
            var Q27;
            Q27=makeQuery(id+"F14.boolean.opBoolean","COPY",EDGE,{"derivedFrom":makeQuery(id+"F14.opExtrude","CAP_EDGE",EDGE,{"disambiguationData":[OSD([sQuery(id+"F13.wireOp",EDGE,"E49.0.16.0")])],"isStart":true})});
            var Q28;
            Q28=makeQuery(id+"F14.boolean.opBoolean","COPY",EDGE,{"derivedFrom":makeQuery(id+"F14.opExtrude","CAP_EDGE",EDGE,{"disambiguationData":[OSD([sQuery(id+"F13.wireOp",EDGE,"E49.0.17.2")])],"isStart":true})});
            var Q29;
            Q29=makeQuery(id+"F14.boolean.opBoolean","COPY",EDGE,{"derivedFrom":makeQuery(id+"F14.opExtrude","CAP_EDGE",EDGE,{"disambiguationData":[OSD([sQuery(id+"F13.wireOp",EDGE,"E49.0.11.0")])],"isStart":true})});
            var Q30;
            Q30=makeQuery(id+"F14.boolean.opBoolean","COPY",EDGE,{"derivedFrom":makeQuery(id+"F14.opExtrude","CAP_EDGE",EDGE,{"disambiguationData":[OSD([sQuery(id+"F13.wireOp",EDGE,"E49.0.11.2")])],"isStart":true})});
            var Q31;
            Q31=makeQuery(id+"F14.boolean.opBoolean","COPY",EDGE,{"derivedFrom":makeQuery(id+"F14.opExtrude","CAP_EDGE",EDGE,{"disambiguationData":[OSD([sQuery(id+"F13.wireOp",EDGE,"E49.0.10.0")])],"isStart":true})});
            var Q32;
            Q32=makeQuery(id+"F14.boolean.opBoolean","COPY",EDGE,{"derivedFrom":makeQuery(id+"F14.opExtrude","CAP_EDGE",EDGE,{"disambiguationData":[OSD([sQuery(id+"F13.wireOp",EDGE,"E49.0.10.2")])],"isStart":true})});
            var Q33;
            Q33=makeQuery(id+"F14.boolean.opBoolean","COPY",EDGE,{"derivedFrom":makeQuery(id+"F14.opExtrude","CAP_EDGE",EDGE,{"disambiguationData":[OSD([sQuery(id+"F13.wireOp",EDGE,"E49.0.9.0")])],"isStart":true})});
            var Q34;
            Q34=makeQuery(id+"F14.boolean.opBoolean","COPY",EDGE,{"derivedFrom":makeQuery(id+"F14.opExtrude","CAP_EDGE",EDGE,{"disambiguationData":[OSD([sQuery(id+"F13.wireOp",EDGE,"E49.0.18.2")])],"isStart":true})});
            var Q35;
            Q35=makeQuery(id+"F14.boolean.opBoolean","COPY",EDGE,{"derivedFrom":makeQuery(id+"F14.opExtrude","CAP_EDGE",EDGE,{"disambiguationData":[OSD([sQuery(id+"F13.wireOp",EDGE,"E49.0.17.0")])],"isStart":true})});
            var Q36;
            Q36=makeQuery(id+"F14.boolean.opBoolean","COPY",EDGE,{"derivedFrom":makeQuery(id+"F14.opExtrude","CAP_EDGE",EDGE,{"disambiguationData":[OSD([sQuery(id+"F13.wireOp",EDGE,"E50.6.0.19")])],"isStart":true})});
            var Q37;
            Q37=makeQuery(id+"F14.boolean.opBoolean","COPY",EDGE,{"derivedFrom":makeQuery(id+"F14.opExtrude","CAP_EDGE",EDGE,{"disambiguationData":[OSD([sQuery(id+"F13.wireOp",EDGE,"E49.0.18.0")])],"isStart":true})});
            var Q38;
            Q38=makeQuery(id+"F14.boolean.opBoolean","COPY",EDGE,{"derivedFrom":makeQuery(id+"F14.opExtrude","CAP_EDGE",EDGE,{"disambiguationData":[OSD([sQuery(id+"F13.wireOp",EDGE,"E50.0.0.19")])],"isStart":true})});
            fillet(context, id + "F15", {"entities" : qUnion([Q0, Q1, Q2, Q3, Q4, Q5, Q6, Q7, Q8, Q9, Q10, Q11, Q12, Q13, Q14, Q15, Q16, Q17, Q18, Q19, Q20, Q21, Q22, Q23, Q24, Q25, Q26, Q27, Q28, Q29, Q30, Q31, Q32, Q33, Q34, Q35, Q36, Q37, Q38]), "radius" : 1 * mm, "tangentPropagation" : true, "allowEdgeOverflow" : false});
        }
        {
            var Q0;
            Q0=makeQuery(id+"F5.boolean.opBoolean","COPY",EDGE,{"derivedFrom":makeQuery(id+"F5.opExtrude","SWEPT_EDGE",EDGE,{"disambiguationData":[OSD([sQuery(id+"F4.wireOp",EDGE,"E2.bottom"),sQuery(id+"F4.wireOp",EDGE,"E2.right")])]})});
            var Q1;
            Q1=makeQuery(id+"F5.boolean.opBoolean","COPY",EDGE,{"derivedFrom":makeQuery(id+"F5.opExtrude","SWEPT_EDGE",EDGE,{"disambiguationData":[OSD([sQuery(id+"F4.wireOp",EDGE,"E2.bottom"),sQuery(id+"F4.wireOp",EDGE,"E2.left")])]})});
            var Q2;
            Q2=makeQuery(id+"F5.boolean.opBoolean","COPY",EDGE,{"derivedFrom":makeQuery(id+"F5.opExtrude","CAP_EDGE",EDGE,{"disambiguationData":[OSD([sQuery(id+"F4.wireOp",EDGE,"E2.bottom")])],"isStart":false})});
            var Q3;
            Q3=makeQuery(id+"F5.boolean.opBoolean","COPY",EDGE,{"derivedFrom":makeQuery(id+"F5.opExtrude","CAP_EDGE",EDGE,{"disambiguationData":[OSD([sQuery(id+"F4.wireOp",EDGE,"E2.left")])],"isStart":false})});
            var Q4;
            Q4=makeQuery(id+"F5.boolean.opBoolean","COPY",EDGE,{"derivedFrom":makeQuery(id+"F5.opExtrude","CAP_EDGE",EDGE,{"disambiguationData":[OSD([sQuery(id+"F4.wireOp",EDGE,"E2.right")])],"isStart":false})});
            var Q5;
            Q5=makeQuery(id+"F5.boolean.opBoolean","COPY",EDGE,{"derivedFrom":makeQuery(id+"F5.opExtrude","CAP_EDGE",EDGE,{"disambiguationData":[OSD([sQuery(id+"F4.wireOp",EDGE,"E2.top")])],"isStart":false})});
            var Q6;
            Q6=makeQuery(id+"F5.boolean.opBoolean","COPY",EDGE,{"derivedFrom":makeQuery(id+"F5.opExtrude","SWEPT_EDGE",EDGE,{"disambiguationData":[OSD([sQuery(id+"F4.wireOp",EDGE,"E2.top"),sQuery(id+"F4.wireOp",EDGE,"E2.right")])]})});
            var Q7;
            Q7=makeQuery(id+"F5.boolean.opBoolean","COPY",EDGE,{"derivedFrom":makeQuery(id+"F5.opExtrude","SWEPT_EDGE",EDGE,{"disambiguationData":[OSD([sQuery(id+"F4.wireOp",EDGE,"E2.top"),sQuery(id+"F4.wireOp",EDGE,"E2.left")])]})});
            var Q8;
            Q8=makeQuery(id+"F2.opExtrude","CAP_EDGE",EDGE,{"disambiguationData":[OSD([sQuery(id+"F1.wireOp",EDGE,"E0.top")])],"isStart":true});
            var Q9;
            Q9=makeQuery(id+"F6.boolean.opBoolean","MERGE",EDGE,{"derivedFrom":[makeQuery(id+"F2.opExtrude","CAP_EDGE",EDGE,{"disambiguationData":[OSD([sQuery(id+"F1.wireOp",EDGE,"E0.right")])],"isStart":true}),makeQuery(id+"F6.opExtrude","SWEPT_EDGE",EDGE,{"disambiguationData":[OSD([sQuery(id+"F3.wireOp",EDGE,"E1.bottom"),sQuery(id+"F3.wireOp",EDGE,"E1.right")])]})]});
            var Q10;
            Q10=makeQuery(id+"F6.boolean.opBoolean","MERGE",EDGE,{"derivedFrom":[makeQuery(id+"F2.opExtrude","CAP_EDGE",EDGE,{"disambiguationData":[OSD([sQuery(id+"F1.wireOp",EDGE,"E0.left")])],"isStart":true}),makeQuery(id+"F6.opExtrude","SWEPT_EDGE",EDGE,{"disambiguationData":[OSD([sQuery(id+"F3.wireOp",EDGE,"E1.bottom"),sQuery(id+"F3.wireOp",EDGE,"E1.left")])]})]});
            var Q11;
            Q11=makeQuery(id+"F6.opExtrude","CAP_EDGE",EDGE,{"disambiguationData":[OSD([sQuery(id+"F3.wireOp",EDGE,"E1.bottom")])],"isStart":false});
            var Q12;
            Q12=makeQuery(id+"F6.opExtrude","CAP_EDGE",EDGE,{"disambiguationData":[OSD([sQuery(id+"F3.wireOp",EDGE,"E1.left")])],"isStart":false});
            var Q13;
            Q13=makeQuery(id+"F2.opExtrude","SWEPT_EDGE",EDGE,{"disambiguationData":[OSD([sQuery(id+"F1.wireOp",EDGE,"E0.top"),sQuery(id+"F1.wireOp",EDGE,"E0.left")])]});
            var Q14;
            Q14=makeQuery(id+"F2.opExtrude","SWEPT_EDGE",EDGE,{"disambiguationData":[OSD([sQuery(id+"F1.wireOp",EDGE,"E0.top"),sQuery(id+"F1.wireOp",EDGE,"E0.right")])]});
            var Q15;
            Q15=makeQuery(id+"F6.opExtrude","CAP_EDGE",EDGE,{"disambiguationData":[OSD([sQuery(id+"F3.wireOp",EDGE,"E1.right")])],"isStart":false});
            fillet(context, id + "F16", {"entities" : qUnion([Q0, Q1, Q2, Q3, Q4, Q5, Q6, Q7, Q8, Q9, Q10, Q11, Q12, Q13, Q14, Q15]), "radius" : 5 * mm, "tangentPropagation" : true, "allowEdgeOverflow" : false});
        }
        {
            var Q0;
            Q0=makeQuery(id+"F6.boolean.opBoolean","MERGE",FACE,{"derivedFrom":[makeQuery(id+"F2.opExtrude","CAP_FACE",FACE,{"disambiguationData":[OSD([sQuery(id+"F1.wireOp",EDGE,"E0.bottom"),sQuery(id+"F1.wireOp",EDGE,"E0.top"),sQuery(id+"F1.wireOp",EDGE,"E0.left"),sQuery(id+"F1.wireOp",EDGE,"E0.right")])],"isStart":true}),makeQuery(id+"F6.opExtrude","SWEPT_FACE",FACE,{"disambiguationData":[OSD([sQuery(id+"F3.wireOp",EDGE,"E1.bottom")])]})]});
            var sketch = newSketch(context, id + "F17", { "sketchPlane" : qUnion([Q0])});
            skCircle(sketch, "E51", {"center": v(0, 0) * mm, "radius": 5 * mm});
            skCircle(sketch, "E52", {"center": v(0, 11) * mm, "radius": 2 * mm});
            skCircle(sketch, "E53", {"center": v(0, 21) * mm, "radius": 3.5 * mm});
            skCircle(sketch, "E54.1.0", {"center": v(-11.35, 17.67) * mm, "radius": 3.5 * mm});
            skCircle(sketch, "E54.2.0", {"center": v(-19.1, 8.72) * mm, "radius": 3.5 * mm});
            skCircle(sketch, "E54.3.0", {"center": v(-20.79, -2.99) * mm, "radius": 3.5 * mm});
            skCircle(sketch, "E54.4.0", {"center": v(-15.87, -13.75) * mm, "radius": 3.5 * mm});
            skCircle(sketch, "E54.5.0", {"center": v(-5.92, -20.15) * mm, "radius": 3.5 * mm});
            skCircle(sketch, "E54.6.0", {"center": v(5.92, -20.15) * mm, "radius": 3.5 * mm});
            skCircle(sketch, "E55.1.0", {"center": v(-8.6, 6.86) * mm, "radius": 2 * mm});
            skCircle(sketch, "E55.2.0", {"center": v(-10.72, -2.45) * mm, "radius": 2 * mm});
            skCircle(sketch, "E55.3.0", {"center": v(-4.77, -9.91) * mm, "radius": 2 * mm});
            skCircle(sketch, "E55.4.0", {"center": v(4.77, -9.91) * mm, "radius": 2 * mm});
            skCircle(sketch, "E55.5.0", {"center": v(10.72, -2.45) * mm, "radius": 2 * mm});
            skCircle(sketch, "E55.6.0", {"center": v(8.6, 6.86) * mm, "radius": 2 * mm});
            skCircle(sketch, "E56.1.7.0", {"center": v(15.87, -13.75) * mm, "radius": 3.5 * mm});
            skCircle(sketch, "E56.1.8.0", {"center": v(20.79, -2.99) * mm, "radius": 3.5 * mm});
            skCircle(sketch, "E57.1.9.0", {"center": v(19.1, 8.72) * mm, "radius": 3.5 * mm});
            skCircle(sketch, "E57.1.10.0", {"center": v(11.35, 17.67) * mm, "radius": 3.5 * mm});
            skSolve(sketch);
        }
        {
            var Q0;
            Q0 = qSketchRegion(id + "F17", true);
            extrude(context, id + "F18", {"entities" : qUnion([Q0]), "operationType" : NewBodyOperationType.REMOVE, "endBound" : BoundingType.UP_TO_NEXT, "oppositeDirection" : true, "depth" : 25 * mm, "offsetDistance" : 25 * mm, "hasDraft" : true, "draftAngle" : 3 * degree, "draftPullDirection" : true});
        }
    });
